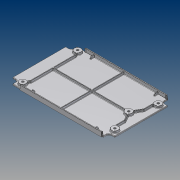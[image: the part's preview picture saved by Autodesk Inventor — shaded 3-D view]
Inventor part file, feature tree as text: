
AUTODESK INVENTOR PART (.ipt)
format: ipt  version: unknown  size: 1,734,144 bytes
history: native  units: mm (DEFAULTED — no unit token found)
features: sketch x7, fillet x7, extrude x6, other x4, plane x3, hole x1, draft x1, pattern_linear x1
ambient origin geometry x5: Origin, X Axis, Y Axis, Z Axis, Center Point
feature tree (30):
  sketch  "Sketch2"  dims[d0=0.79375mm d1=209.55mm]
  extrude  "Extrusion1"  Depth=209.55mm
  extrude  "Extrusion3"  Depth=223.393mm
  hole  "Hole1"  [1 undecoded]
  draft  "FaceDraft1"
  extrude  "Side Wings"  Depth=4.4704mm TaperAngle=0.0deg
  other  "Side Wing End Draft"
  other  "Side Wing Inside Draft"
  other  "Ribs"
  extrude  "Rib Shaping"  Depth=2.54mm
  pattern_linear  "Rib Shaping Pattern"  Count1=12  [1 undecoded]
  extrude  "Side Wing Tips"  TaperAngle=0.0deg  [1 undecoded]
  other  "Side Wing Tips Draft"
  extrude  "Velcro Cut"  Depth=17.272mm
  fillet  "Rib Joining Fillets"  Radius=40.0mm
  fillet  "Fillet5"  Radius=55.0mm
  fillet  "Fillet6"  Radius=10.0mm
  fillet  "Top Fillets"  Radius=44.5mm
  fillet  "Bottom Fillets"  Radius=172.0mm
  fillet  "Velcro Corner Fillet"  Radius=0.349066mm
  fillet  "Velcro Edge Fillet"  Radius=0.79375mm
  plane  "YZ Plane (RIGHT)"
  plane  "XZ Plane (TOP)"
  plane  "XY Plane (FRONT)"
  sketch  "Sketch4"  dims[d2=127.0mm d4=223.393mm]
  sketch  "Sketch5"  dims[d5=140.843mm d6=2.54mm d7=0.349066mm]
  sketch  "Sketch6"  dims[d13=5.5626mm d14=4.4704mm d15=0.0mm]
  sketch  "Sketch7"  dims[d16=5.4864mm d17=12.7mm d18=10.6172mm d19=4.4704mm d20=14.3117mm d21=19.05mm d22=20.594885mm d23=2.54mm]
  sketch  "Sketch8"  dims[d25=17.0mm]
  sketch  "Sketch9"  dims[d26=95.0mm d27=120.0mm d28=0.0mm d29=17.272mm d30=40.0mm d31=55.0mm d32=10.0mm d33=44.5mm d34=172.0mm d35=0.349066mm d36=0.79375mm d37=1.27mm d38=1.27mm d39=1.27mm d40=0.396875mm d41=0.79375mm d42=26.67mm d43=101.6mm d44=1.27mm d46=1.27mm d47=-7.853982mm d48=3.175mm d49=1.5875mm d50=143.8656mm d51=3.048mm d52=9.398mm d53=-0.523599mm d54=-0.698132mm d55=96.8502mm d56=82.3722mm d57=98.4504mm d58=80.6704mm d59=0.396875mm d61=1.778mm d62=2.54mm d63=0.349066mm d64=139.7mm d66=123.19mm d67=0.174533mm d68=45.0deg d69=1.5875mm d70=1.5875mm d71=25.4mm d72=0.0mm d73=139.7mm d74=139.7mm d75=25.4mm d76=0.349066mm d78=1.27mm d79=0.359413mm d80=0.174533mm d85=0.359413mm d86=30.0deg d87=1.27mm d88=0.508mm d90=1.27mm d91=1.27mm d92=0.508mm d93=1.27mm d94=1.27mm d95=0.79375mm d97=0.396875mm d100=0.79375mm d105=0.254mm d110=26.543mm d111=91.2mm d112=166.243mm d113=6.35mm d114=60.0deg d115=184.15mm d116=20.0mm d118=139.7mm d119=1.016mm d120=3.048mm d121=60.325mm]
note: 3 required parameter values undecoded (feature->parameter linkage not recoverable at this tier; creation-order binding heuristic only, values carry confidence <= 0.55)
